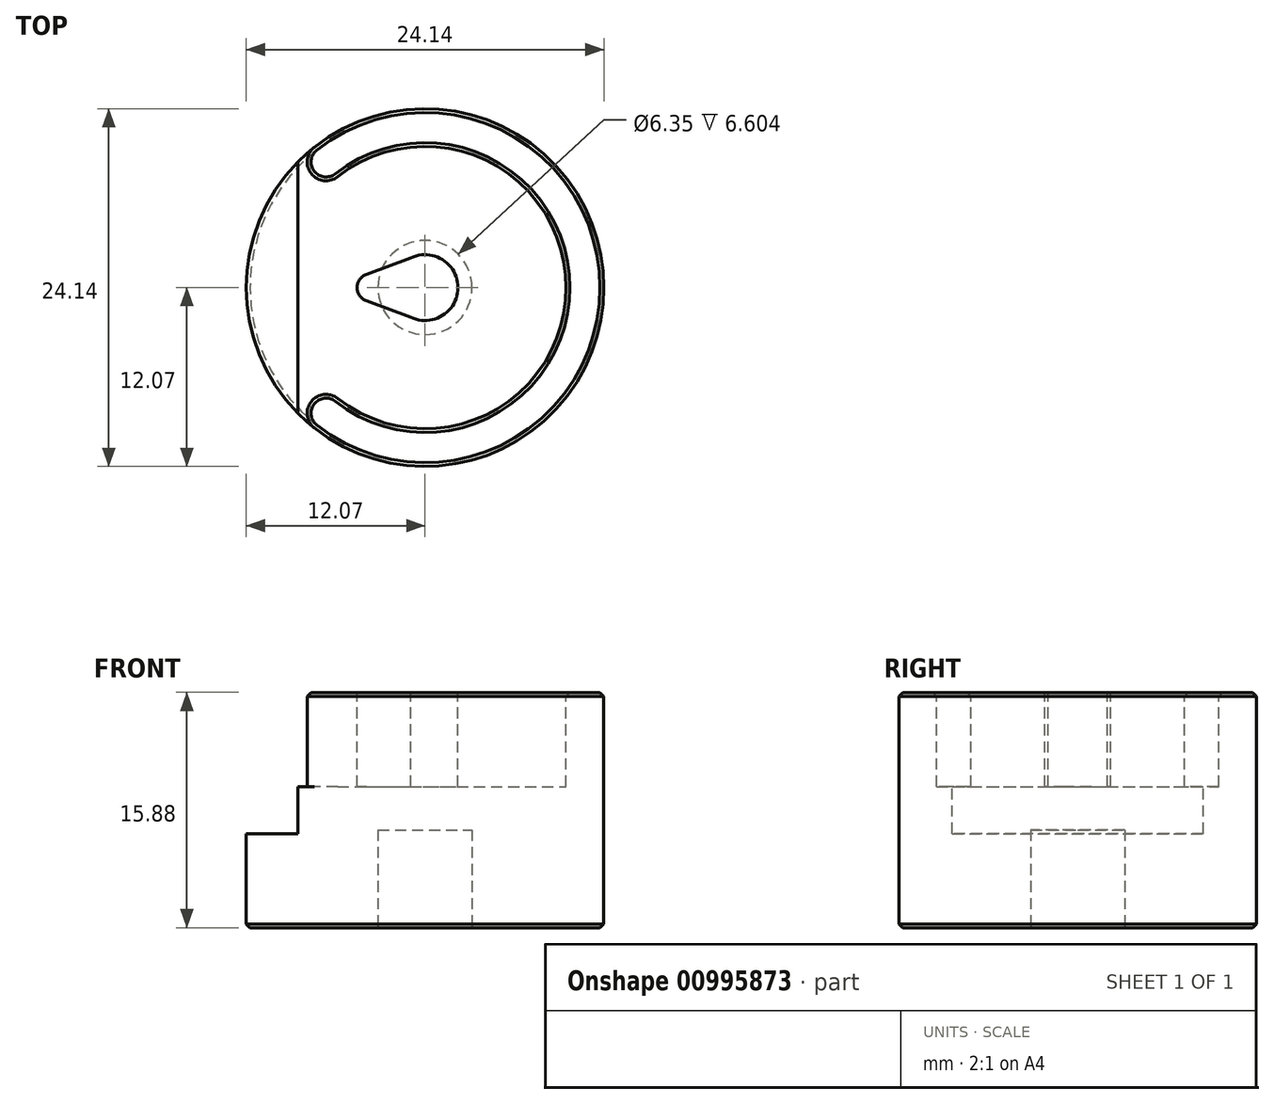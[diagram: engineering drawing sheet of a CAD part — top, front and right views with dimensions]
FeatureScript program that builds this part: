
annotation { "Feature Type Name" : "Feature", "Feature Type Description" : "" }
export const myFeature = defineFeature(function(context is Context, id is Id, definition is map)
    precondition{}
    {
        {
            var Q0;
            Q0=qCreatedBy(makeId("Top.planeOp"),FACE);
            var sketch = newSketch(context, id + "F0", { "sketchPlane" : qUnion([Q0])});
            skCircle(sketch, "E0", {"center": v(0, 0) * mm, "radius": 12.07 * mm});
            skSolve(sketch);
        }
        {
            var Q0;
            Q0=makeQuery(id+"F0.imprint","IMPRINT",FACE,{"disambiguationData":[TD([[makeQuery(id+"F0.imprint","IMPRINT",EDGE,{"derivedFrom":sQuery(id+"F0.wireOp",EDGE,"E0")}),1.0]])]});
            extrude(context, id + "F1", {"entities" : qUnion([Q0]), "depth" : 15.88 * mm, "offsetDistance" : 25.4 * mm});
        }
        {
            var Q0;
            Q0=makeQuery(id+"F1.opExtrude","CAP_FACE",FACE,{"disambiguationData":[OSD([sQuery(id+"F0.wireOp",EDGE,"E0")])],"isStart":false});
            var sketch = newSketch(context, id + "F2", { "sketchPlane" : qUnion([Q0])});
            skArc(sketch, "E1", {"start": v(-0.97, -2) * mm, "mid": v(2.22, 0) * mm, "end": v(-0.97, 2) * mm});
            skArc(sketch, "E2", {"start": v(-3.96, 0.9) * mm, "mid": v(-4.58, 0) * mm, "end": v(-3.96, -0.9) * mm});
            skLineSegment(sketch, "E3", {"start": v(-3.96, 0.9) * mm, "end": v(-0.57, 2.15) * mm});
            skLineSegment(sketch, "E4.MirrorCS", {"start": v(-3.96, -0.9) * mm, "end": v(-0.57, -2.15) * mm});
            skArc(sketch, "E5", {"start": v(-5.9, -7.48) * mm, "mid": v(9.53, 0) * mm, "end": v(-5.9, 7.48) * mm});
            skArc(sketch, "E6", {"start": v(-5.9, -7.48) * mm, "mid": v(-7.68, -7.7) * mm, "end": v(-7.47, -9.48) * mm});
            skArc(sketch, "E7.MirrorCS", {"start": v(-5.9, 7.48) * mm, "mid": v(-7.68, 7.7) * mm, "end": v(-7.47, 9.48) * mm});
            skPoint(sketch, "E8", {"position": v(-8.59, 0) * mm});
            skLineSegment(sketch, "E9", {"start": v(-8.59, -8.48) * mm, "end": v(-8.59, 8.48) * mm});
            skCircle(sketch, "E10.0", {"center": v(0, 0) * mm, "radius": 12.07 * mm});
            skSolve(sketch);
        }
        {
            var Q0;
            {var subQ5=sQuery(id+"F2.wireOp",EDGE,"E2");Q0=makeQuery(id+"F2.imprint","IMPRINT",FACE,{"disambiguationData":[TD([[makeQuery(id+"F2.imprint","IMPRINT",EDGE,{"derivedFrom":subQ5}),-1.0]])]});}
            extrude(context, id + "F3", {"entities" : qUnion([Q0]), "operationType" : NewBodyOperationType.REMOVE, "oppositeDirection" : true, "depth" : 6.35 * mm, "offsetDistance" : 25.4 * mm});
        }
        {
            var Q0;
            {var subQ0=sQuery(id+"F0.wireOp",EDGE,"E0");Q0=makeQuery(id+"F3.boolean.opBoolean","SPLIT",FACE,{"disambiguationData":[TD([makeQuery(id+"F3.opExtrude","SWEPT_FACE",FACE,{"disambiguationData":[OSD([sQuery(id+"F2.wireOp",EDGE,"E9")])]})])],"derivedFrom":makeQuery(id+"F1.opExtrude","CAP_FACE",FACE,{"disambiguationData":[OSD([subQ0])],"isStart":false})});}
            extrude(context, id + "F4", {"entities" : qUnion([Q0]), "operationType" : NewBodyOperationType.REMOVE, "oppositeDirection" : true, "depth" : 9.52 * mm, "offsetDistance" : 25.4 * mm});
        }
        {
            var Q0;
            Q0=makeQuery(id+"F1.opExtrude","CAP_FACE",FACE,{"disambiguationData":[OSD([sQuery(id+"F0.wireOp",EDGE,"E0")])],"isStart":true});
            var sketch = newSketch(context, id + "F5", { "sketchPlane" : qUnion([Q0])});
            skCircle(sketch, "E11", {"center": v(0, 0) * mm, "radius": 3.18 * mm});
            skSolve(sketch);
        }
        {
            var Q0;
            Q0=makeQuery(id+"F5.imprint","IMPRINT",FACE,{"disambiguationData":[TD([[makeQuery(id+"F5.imprint","IMPRINT",EDGE,{"derivedFrom":sQuery(id+"F5.wireOp",EDGE,"E11")}),1.0]])]});
            extrude(context, id + "F6", {"entities" : qUnion([Q0]), "operationType" : NewBodyOperationType.REMOVE, "oppositeDirection" : true, "depth" : 6.6 * mm, "offsetDistance" : 25.4 * mm});
        }
        {
            var Q0;
            {var subQ0=sQuery(id+"F0.wireOp",EDGE,"E0");Q0=makeQuery(id+"F3.boolean.opBoolean","SPLIT",EDGE,{"disambiguationData":[TD([makeQuery(id+"F3.opExtrude","SWEPT_FACE",FACE,{"disambiguationData":[OSD([sQuery(id+"F2.wireOp",EDGE,"E6")])]})])],"derivedFrom":makeQuery(id+"F1.opExtrude","CAP_EDGE",EDGE,{"disambiguationData":[OSD([subQ0])],"isStart":false})});}
            var Q1;
            Q1=makeQuery(id+"F3.boolean.opBoolean","COPY",EDGE,{"derivedFrom":makeQuery(id+"F3.opExtrude","CAP_EDGE",EDGE,{"disambiguationData":[OSD([sQuery(id+"F2.wireOp",EDGE,"E5")])],"isStart":true})});
            var Q2;
            Q2=makeQuery(id+"F3.boolean.opBoolean","COPY",EDGE,{"derivedFrom":makeQuery(id+"F3.opExtrude","CAP_EDGE",EDGE,{"disambiguationData":[OSD([sQuery(id+"F2.wireOp",EDGE,"E6")])],"isStart":true})});
            var Q3;
            Q3=makeQuery(id+"F3.boolean.opBoolean","COPY",EDGE,{"derivedFrom":makeQuery(id+"F3.opExtrude","CAP_EDGE",EDGE,{"disambiguationData":[OSD([sQuery(id+"F2.wireOp",EDGE,"E7.MirrorCS")])],"isStart":true})});
            var Q4;
            Q4=makeQuery(id+"F3.boolean.opBoolean","COPY",EDGE,{"derivedFrom":makeQuery(id+"F3.opExtrude","CAP_EDGE",EDGE,{"disambiguationData":[OSD([sQuery(id+"F2.wireOp",EDGE,"E9")])],"isStart":false})});
            var Q5;
            Q5=makeQuery(id+"F4.boolean.opBoolean","COPY",EDGE,{"derivedFrom":makeQuery(id+"F4.opExtrude","CAP_EDGE",EDGE,{"disambiguationData":[OSD([sQuery(id+"F0.wireOp",EDGE,"E0")])],"isStart":false})});
            var Q6;
            {var subQ0=sQuery(id+"F2.wireOp",EDGE,"E10.0");Q6=makeQuery(id+"F3.boolean.opBoolean","COPY",EDGE,{"derivedFrom":makeQuery(id+"F3.opExtrude","CAP_EDGE",EDGE,{"disambiguationData":[OSD([subQ0]),TDD([makeQuery(id+"F2.imprint","IMPRINT",EDGE,{"disambiguationData":[TD([[makeQuery(id+"F2.imprint","INTERSECT",VERTEX,{"derivedFrom":[sQuery(id+"F2.wireOp",EDGE,"E6"),subQ0]}),1.0]])],"derivedFrom":subQ0})])],"isStart":false})});}
            var Q7;
            {var subQ0=sQuery(id+"F2.wireOp",EDGE,"E10.0");Q7=makeQuery(id+"F3.boolean.opBoolean","COPY",EDGE,{"derivedFrom":makeQuery(id+"F3.opExtrude","CAP_EDGE",EDGE,{"disambiguationData":[OSD([subQ0]),TDD([makeQuery(id+"F2.imprint","IMPRINT",EDGE,{"disambiguationData":[TD([[makeQuery(id+"F2.imprint","INTERSECT",VERTEX,{"derivedFrom":[sQuery(id+"F2.wireOp",EDGE,"E7.MirrorCS"),subQ0]}),-1.0]])],"derivedFrom":subQ0})])],"isStart":false})});}
            var Q8;
            Q8=makeQuery(id+"F1.opExtrude","CAP_EDGE",EDGE,{"disambiguationData":[OSD([sQuery(id+"F0.wireOp",EDGE,"E0")])],"isStart":true});
            chamfer(context, id + "F7", {"entities" : qUnion([Q0, Q1, Q2, Q3, Q4, Q5, Q6, Q7, Q8]), "width" : 0.25 * mm, "tangentPropagation" : true});
        }
    });
